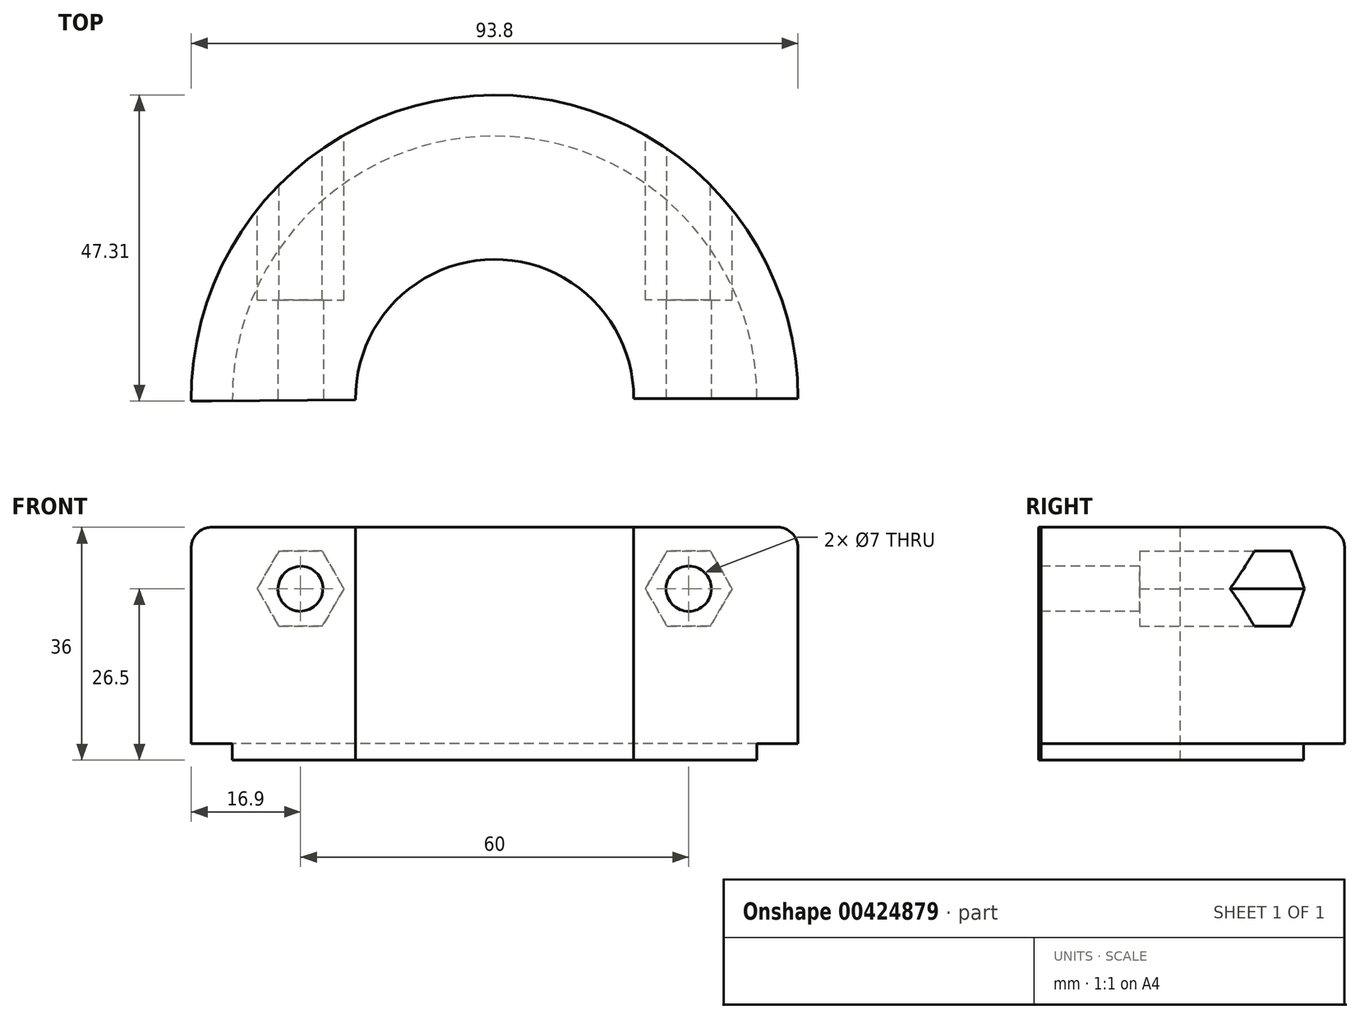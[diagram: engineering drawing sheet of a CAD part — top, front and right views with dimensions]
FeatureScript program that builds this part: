
annotation { "Feature Type Name" : "Feature", "Feature Type Description" : "" }
export const myFeature = defineFeature(function(context is Context, id is Id, definition is map)
    precondition{}
    {
        {
            var Q0;
            Q0=qCreatedBy(makeId("Front.planeOp"),FACE);
            var sketch = newSketch(context, id + "F0", { "sketchPlane" : qUnion([Q0])});
            skLineSegment(sketch, "E0", {"start": v(0, 89.36) * mm, "end": v(0, -89.36) * mm, "construction": true});
            skLineSegment(sketch, "E1.top", {"start": v(21.5, 0) * mm, "end": v(40.55, 0) * mm});
            skPoint(sketch, "E2.visualSharp", {"position": v(46.9, 2.54) * mm});
            skLineSegment(sketch, "E3", {"start": v(40.55, 2.54) * mm, "end": v(46.9, 2.54) * mm});
            skLineSegment(sketch, "E4", {"start": v(46.9, 32.83) * mm, "end": v(46.9, 2.54) * mm});
            skLineSegment(sketch, "E5", {"start": v(21.5, 36) * mm, "end": v(43.73, 36) * mm});
            skLineSegment(sketch, "E6", {"start": v(40.55, 0) * mm, "end": v(40.55, 2.54) * mm});
            skLineSegment(sketch, "E7", {"start": v(-84.1, 0) * mm, "end": v(89.61, 0) * mm, "construction": true});
            skLineSegment(sketch, "E8", {"start": v(21.5, 0) * mm, "end": v(21.5, 36) * mm});
            skPoint(sketch, "E9.visualSharp", {"position": v(46.9, 36) * mm});
            skArc(sketch, "E9.filletArc", {"start": v(46.9, 32.83) * mm, "mid": v(45.97, 35.07) * mm, "end": v(43.73, 36) * mm});
            skSolve(sketch);
        }
        {
            var Q0;
            Q0=makeQuery(id+"F0.imprint","IMPRINT",FACE,{"disambiguationData":[TD([[makeQuery(id+"F0.imprint","IMPRINT",EDGE,{"derivedFrom":sQuery(id+"F0.wireOp",EDGE,"E1.top")}),1.0]])]});
            var Q1;
            Q1=qSketchRegion(id+"F2",true);
            var Q2;
            Q2=sQuery(id+"F0.wireOp",EDGE,"E0");
            revolve(context, id + "F1", {"entities" : qUnion([Q0, Q1]), "axis" : qUnion([Q2]), "revolveType" : RevolveType.TWO_DIRECTIONS, "angle" : 0 * degree, "angleBack" : 179.5 * degree});
        }
        {
            var Q0;
            Q0=qCreatedBy(makeId("Front.planeOp"),FACE);
            var sketch = newSketch(context, id + "F2", { "sketchPlane" : qUnion([Q0])});
            skLineSegment(sketch, "E10", {"start": v(0, 81.52) * mm, "end": v(0, -79.68) * mm, "construction": true});
            skCircle(sketch, "E11", {"center": v(30, 26.5) * mm, "radius": 3.5 * mm});
            skCircle(sketch, "E12.MirrorC", {"center": v(-30, 26.5) * mm, "radius": 3.5 * mm});
            skSolve(sketch);
        }
        {
            var Q0;
            Q0=qSketchRegion(id+"F2",true);
            extrude(context, id + "F3", {"entities" : qUnion([Q0]), "operationType" : NewBodyOperationType.REMOVE, "oppositeDirection" : true, "depth" : 53.34 * mm, "hasSecondDirection" : true, "secondDirectionOppositeDirection" : false, "secondDirectionDepth" : 2.54 * mm});
        }
        {
            var Q0;
            Q0=qCreatedBy(makeId("Front.planeOp"),FACE);
            cPlane(context, id + "F4", {"entities" : qUnion([Q0]), "cplaneType" : CPlaneType.OFFSET, "offset" : 50.8 * mm, "oppositeDirection" : true, "width" : 152.4 * mm, "height" : 152.4 * mm});
        }
        {
            var Q0;
            Q0=qCreatedBy(id+"F4.planeOp",FACE);
            var sketch = newSketch(context, id + "F5", { "sketchPlane" : qUnion([Q0])});
            skLineSegment(sketch, "E13", {"start": v(0, 83.45) * mm, "end": v(0, -83.48) * mm, "construction": true});
            skPoint(sketch, "E14", {"position": v(30, 26.5) * mm});
            skCircle(sketch, "E15.cCircle", {"center": v(30, 26.5) * mm, "radius": 5.8 * mm, "construction": true});
            skLineSegment(sketch, "E15.0", {"start": v(33.35, 32.3) * mm, "end": v(36.7, 26.5) * mm});
            skLineSegment(sketch, "E15.1", {"start": v(36.7, 26.5) * mm, "end": v(33.35, 20.7) * mm});
            skLineSegment(sketch, "E15.2", {"start": v(33.35, 20.7) * mm, "end": v(26.65, 20.7) * mm});
            skLineSegment(sketch, "E15.3", {"start": v(26.65, 20.7) * mm, "end": v(23.3, 26.5) * mm});
            skLineSegment(sketch, "E15.4", {"start": v(23.3, 26.5) * mm, "end": v(26.65, 32.3) * mm});
            skLineSegment(sketch, "E15.5", {"start": v(26.65, 32.3) * mm, "end": v(33.35, 32.3) * mm});
            skPoint(sketch, "E15.0.midPoint", {"position": v(35.02, 29.4) * mm});
            skPoint(sketch, "E16", {"position": v(-30, 26.5) * mm});
            skCircle(sketch, "E17.cCircle", {"center": v(-30, 26.5) * mm, "radius": 5.8 * mm, "construction": true});
            skLineSegment(sketch, "E17.0", {"start": v(-36.7, 26.5) * mm, "end": v(-33.35, 32.3) * mm});
            skLineSegment(sketch, "E17.1", {"start": v(-33.35, 32.3) * mm, "end": v(-26.65, 32.3) * mm});
            skLineSegment(sketch, "E17.2", {"start": v(-26.65, 32.3) * mm, "end": v(-23.3, 26.5) * mm});
            skLineSegment(sketch, "E17.3", {"start": v(-23.3, 26.5) * mm, "end": v(-26.65, 20.7) * mm});
            skLineSegment(sketch, "E17.4", {"start": v(-26.65, 20.7) * mm, "end": v(-33.35, 20.7) * mm});
            skLineSegment(sketch, "E17.5", {"start": v(-33.35, 20.7) * mm, "end": v(-36.7, 26.5) * mm});
            skPoint(sketch, "E17.0.midPoint", {"position": v(-35.02, 29.4) * mm});
            skSolve(sketch);
        }
        {
            var Q0;
            Q0=makeQuery(id+"F5.imprint","IMPRINT",FACE,{"disambiguationData":[TD([[makeQuery(id+"F5.imprint","IMPRINT",EDGE,{"derivedFrom":sQuery(id+"F5.wireOp",EDGE,"E15.0")}),-1.0]])]});
            var Q1;
            Q1=makeQuery(id+"F5.imprint","IMPRINT",FACE,{"disambiguationData":[TD([[makeQuery(id+"F5.imprint","IMPRINT",EDGE,{"derivedFrom":sQuery(id+"F5.wireOp",EDGE,"E17.0")}),-1.0]])]});
            var Q2;
            Q2 = qSketchRegion(id + "FJtj0piFx7HUNcg_1", true);
            extrude(context, id + "F6", {"entities" : qUnion([Q0, Q1, Q2]), "operationType" : NewBodyOperationType.REMOVE, "depth" : 35.56 * mm});
        }
    });
